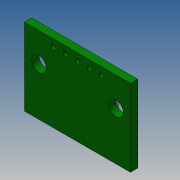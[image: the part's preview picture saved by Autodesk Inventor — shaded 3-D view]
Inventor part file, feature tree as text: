
AUTODESK INVENTOR PART (.ipt)
format: ipt  version: 2017 (Build 210142000, 142)  size: 842,240 bytes
history: native  units: mm
features: other x11, extrude x1, sketch x1
ambient origin geometry x8: Origin, YZ Plane, XZ Plane, XY Plane, X Axis, Y Axis, Z Axis, Center Point
bodies: Body1 (feature_tree), Body2 (feature_tree), Body3 (feature_tree)
feature tree (13):
  other  "MINIUSBSHELL.ipt"
  other  "MINIUSBCORE.ipt"
  other  "Desplazar cuerpo1"
  other  "Desplazar cuerpo2"
  extrude  "Extrusión1"  Depth=10.0mm
  other  "Solid1::MINIUSBSHELL.ipt"
  other  "OperaciónIdentificador1"
  other  "Solid1::MINIUSBCORE.ipt"
  other  "OperaciónIdentificador2"
  sketch  "Boceto1"  dims[d0=10.0mm d1=10.0mm d2=180.0deg d3=0.0mm d4=0.0mm d5=7.0mm d6=1.5mm d7=0.0mm d8=0.7mm d9=0.98998mm d10=50.0mm d12=2.5mm d13=10.0mm d15=10.0mm d17=1.5mm d18=3.0mm d19=22.0mm d20=3.0mm d21=16.0mm d22=16.0mm d23=10.0mm]
  other  "Sólido3"
  other  "Sólido1"
  other  "Sólido2"
